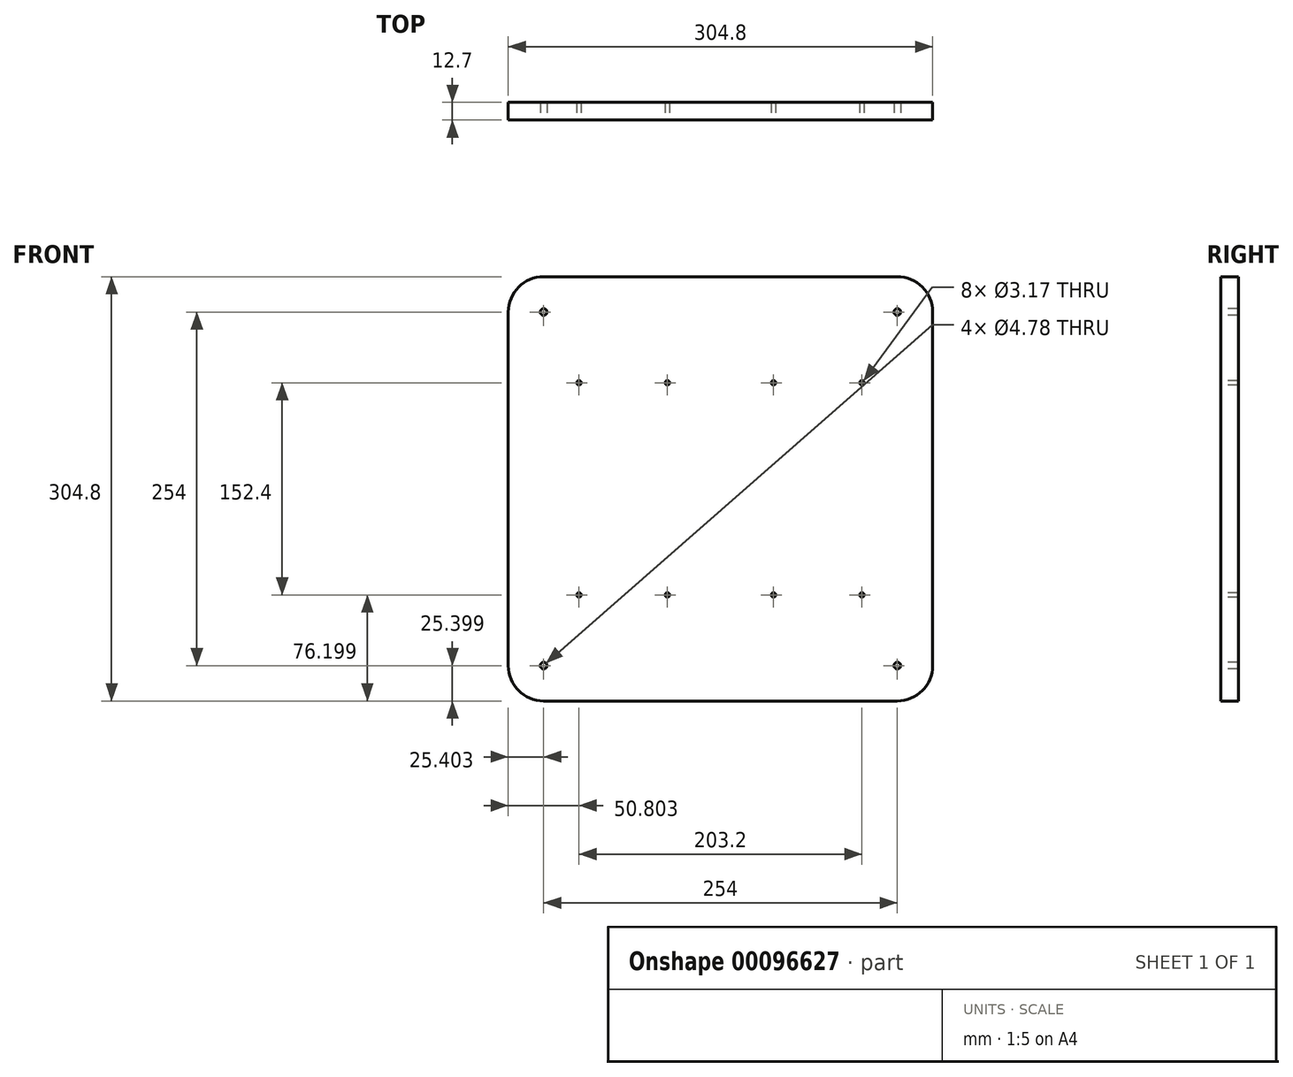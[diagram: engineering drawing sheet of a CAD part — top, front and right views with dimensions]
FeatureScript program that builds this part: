
annotation { "Feature Type Name" : "Feature", "Feature Type Description" : "" }
export const myFeature = defineFeature(function(context is Context, id is Id, definition is map)
    precondition{}
    {
        {
            var Q0;
            Q0=qCreatedBy(makeId("Front.planeOp"),FACE);
            var sketch = newSketch(context, id + "F0", { "sketchPlane" : qUnion([Q0])});
            skLineSegment(sketch, "E0.bottom", {"start": v(-151.46, 183.8) * mm, "end": v(153.34, 183.8) * mm});
            skLineSegment(sketch, "E0.top", {"start": v(-151.46, -121) * mm, "end": v(153.34, -121) * mm});
            skLineSegment(sketch, "E0.left", {"start": v(-151.46, 183.8) * mm, "end": v(-151.46, -121) * mm});
            skLineSegment(sketch, "E0.right", {"start": v(153.34, 183.8) * mm, "end": v(153.34, -121) * mm});
            skSolve(sketch);
        }
        {
            var Q0;
            Q0=makeQuery(id+"F0.imprint","IMPRINT",FACE,{"disambiguationData":[TD([[makeQuery(id+"F0.imprint","IMPRINT",EDGE,{"derivedFrom":sQuery(id+"F0.wireOp",EDGE,"E0.bottom")}),-1.0]])]});
            extrude(context, id + "F1", {"entities" : qUnion([Q0]), "depth" : 12.7 * mm});
        }
        {
            var Q0;
            Q0=makeQuery(id+"F1.opExtrude","SWEPT_EDGE",EDGE,{"disambiguationData":[OSD([sQuery(id+"F0.wireOp",EDGE,"E0.bottom"),sQuery(id+"F0.wireOp",EDGE,"E0.left")])]});
            var Q1;
            Q1=makeQuery(id+"F1.opExtrude","SWEPT_EDGE",EDGE,{"disambiguationData":[OSD([sQuery(id+"F0.wireOp",EDGE,"E0.top"),sQuery(id+"F0.wireOp",EDGE,"E0.left")])]});
            var Q2;
            Q2=makeQuery(id+"F1.opExtrude","SWEPT_EDGE",EDGE,{"disambiguationData":[OSD([sQuery(id+"F0.wireOp",EDGE,"E0.top"),sQuery(id+"F0.wireOp",EDGE,"E0.right")])]});
            var Q3;
            Q3=makeQuery(id+"F1.opExtrude","SWEPT_EDGE",EDGE,{"disambiguationData":[OSD([sQuery(id+"F0.wireOp",EDGE,"E0.bottom"),sQuery(id+"F0.wireOp",EDGE,"E0.right")])]});
            fillet(context, id + "F2", {"entities" : qUnion([Q0, Q1, Q2, Q3]), "radius" : 25.4 * mm, "tangentPropagation" : true, "allowEdgeOverflow" : false});
        }
        {
            var Q0;
            Q0=makeQuery(id+"F1.opExtrude","CAP_FACE",FACE,{"disambiguationData":[OSD([sQuery(id+"F0.wireOp",EDGE,"E0.bottom"),sQuery(id+"F0.wireOp",EDGE,"E0.top"),sQuery(id+"F0.wireOp",EDGE,"E0.left"),sQuery(id+"F0.wireOp",EDGE,"E0.right")])],"isStart":false});
            var sketch = newSketch(context, id + "F3", { "sketchPlane" : qUnion([Q0])});
            skPoint(sketch, "E1", {"position": v(-100.66, -44.8) * mm});
            skPoint(sketch, "E2", {"position": v(-37.16, -44.8) * mm});
            skPoint(sketch, "E3", {"position": v(39.04, -44.8) * mm});
            skPoint(sketch, "E4", {"position": v(102.54, -44.8) * mm});
            skPoint(sketch, "E5", {"position": v(-100.66, 107.6) * mm});
            skPoint(sketch, "E6", {"position": v(-37.16, 107.6) * mm});
            skPoint(sketch, "E7", {"position": v(39.04, 107.6) * mm});
            skPoint(sketch, "E8", {"position": v(102.54, 107.6) * mm});
            skSolve(sketch);
        }
        {
            var Q0;
            Q0=sQuery(id+"F3.wireOp",VERTEX,"E5");
            var Q1;
            Q1=sQuery(id+"F3.wireOp",VERTEX,"E6");
            var Q2;
            Q2=sQuery(id+"F3.wireOp",VERTEX,"E7");
            var Q3;
            Q3=sQuery(id+"F3.wireOp",VERTEX,"E8");
            var Q4;
            Q4=sQuery(id+"F3.wireOp",VERTEX,"E4");
            var Q5;
            Q5=sQuery(id+"F3.wireOp",VERTEX,"E3");
            var Q6;
            Q6=sQuery(id+"F3.wireOp",VERTEX,"E2");
            var Q7;
            Q7=sQuery(id+"F3.wireOp",VERTEX,"E1");
            var Q8;
            Q8=makeQuery(id+"F1.opExtrude","SWEPT_BODY",BODY,{"disambiguationData":[OSD([sQuery(id+"F0.wireOp",EDGE,"E0.bottom"),sQuery(id+"F0.wireOp",EDGE,"E0.top"),sQuery(id+"F0.wireOp",EDGE,"E0.left"),sQuery(id+"F0.wireOp",EDGE,"E0.right")])]});
            hole(context, id + "F4", {"style" : HoleStyle.SIMPLE, "endStyle" : HoleEndStyle.THROUGH, "holeDiameter" : 3.17 * mm, "locations" : qUnion([Q0, Q1, Q2, Q3, Q4, Q5, Q6, Q7]), "scope" : qUnion([Q8]), "isTappedThrough" : true});
        }
        {
            var Q0;
            Q0=makeQuery(id+"F1.opExtrude","CAP_FACE",FACE,{"disambiguationData":[OSD([sQuery(id+"F0.wireOp",EDGE,"E0.bottom"),sQuery(id+"F0.wireOp",EDGE,"E0.top"),sQuery(id+"F0.wireOp",EDGE,"E0.left"),sQuery(id+"F0.wireOp",EDGE,"E0.right")])],"isStart":false});
            var sketch = newSketch(context, id + "F5", { "sketchPlane" : qUnion([Q0])});
            skPoint(sketch, "E9", {"position": v(-126.06, -95.6) * mm});
            skPoint(sketch, "E10", {"position": v(-126.06, 158.4) * mm});
            skPoint(sketch, "E11", {"position": v(127.94, 158.4) * mm});
            skPoint(sketch, "E12", {"position": v(127.94, -95.6) * mm});
            skSolve(sketch);
        }
        {
            var Q0;
            Q0=sQuery(id+"F5.wireOp",VERTEX,"E10");
            var Q1;
            Q1=sQuery(id+"F5.wireOp",VERTEX,"E11");
            var Q2;
            Q2=sQuery(id+"F5.wireOp",VERTEX,"E12");
            var Q3;
            Q3=sQuery(id+"F5.wireOp",VERTEX,"E9");
            var Q4;
            Q4=makeQuery(id+"F1.opExtrude","SWEPT_BODY",BODY,{"disambiguationData":[OSD([sQuery(id+"F0.wireOp",EDGE,"E0.bottom"),sQuery(id+"F0.wireOp",EDGE,"E0.top"),sQuery(id+"F0.wireOp",EDGE,"E0.left"),sQuery(id+"F0.wireOp",EDGE,"E0.right")])]});
            hole(context, id + "F6", {"style" : HoleStyle.SIMPLE, "endStyle" : HoleEndStyle.THROUGH, "holeDiameter" : 4.78 * mm, "locations" : qUnion([Q0, Q1, Q2, Q3]), "scope" : qUnion([Q4]), "isTappedThrough" : true});
        }
    });
